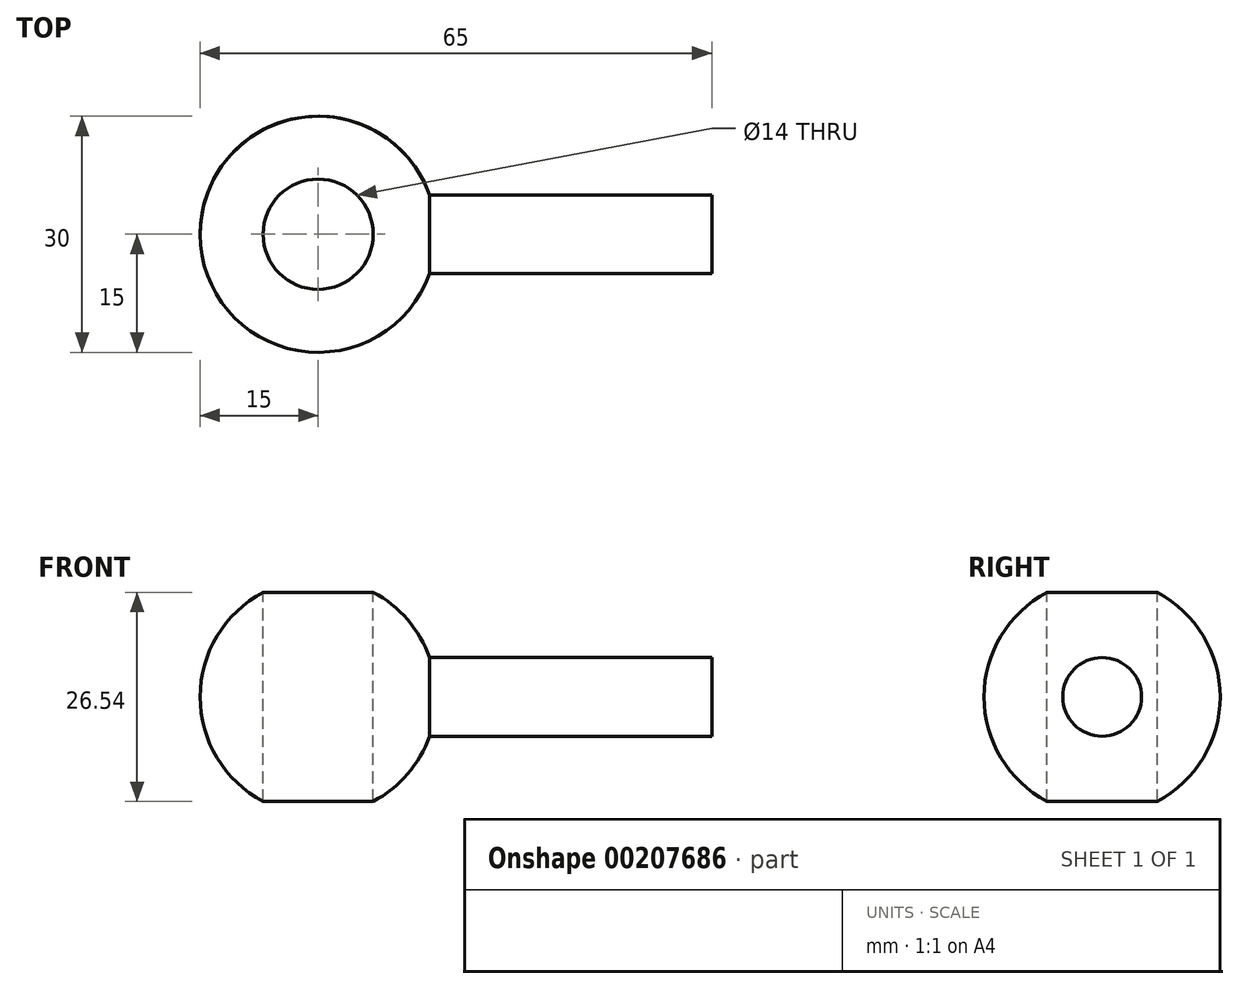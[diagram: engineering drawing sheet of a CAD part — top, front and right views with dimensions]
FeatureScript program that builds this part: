
annotation { "Feature Type Name" : "Feature", "Feature Type Description" : "" }
export const myFeature = defineFeature(function(context is Context, id is Id, definition is map)
    precondition{}
    {
        {
            var Q0;
            Q0=qCreatedBy(makeId("Top.planeOp"),FACE);
            var sketch = newSketch(context, id + "F0", { "sketchPlane" : qUnion([Q0])});
            skArc(sketch, "E0", {"start": v(15, 0) * mm, "mid": v(0, 15) * mm, "end": v(-15, 0) * mm});
            skLineSegment(sketch, "E1", {"start": v(0, 0) * mm, "end": v(50, 0) * mm});
            skLineSegment(sketch, "E2", {"start": v(50, 5) * mm, "end": v(50, 0) * mm});
            skLineSegment(sketch, "E3", {"start": v(50, 5) * mm, "end": v(14.14, 5) * mm});
            skLineSegment(sketch, "E4", {"start": v(-15, 0) * mm, "end": v(0, 0) * mm});
            skSolve(sketch);
        }
        {
            var Q0;
            {var subQ4=sQuery(id+"F0.wireOp",EDGE,"E4");Q0=makeQuery(id+"F0.imprint","IMPRINT",FACE,{"disambiguationData":[TD([[makeQuery(id+"F0.imprint","IMPRINT",EDGE,{"derivedFrom":subQ4}),1.0]])]});}
            var Q1;
            {var subQ4=sQuery(id+"F0.wireOp",EDGE,"E2");Q1=makeQuery(id+"F0.imprint","IMPRINT",FACE,{"disambiguationData":[TD([[makeQuery(id+"F0.imprint","IMPRINT",EDGE,{"derivedFrom":subQ4}),-1.0]])]});}
            var Q2;
            Q2=sQuery(id+"F0.wireOp",EDGE,"E1");
            revolve(context, id + "F1", {"entities" : qUnion([Q0, Q1]), "axis" : qUnion([Q2]), "revolveType" : RevolveType.FULL});
        }
        {
            var Q0;
            Q0=qCreatedBy(makeId("Top.planeOp"),FACE);
            var sketch = newSketch(context, id + "F2", { "sketchPlane" : qUnion([Q0])});
            skCircle(sketch, "E5", {"center": v(0, 0) * mm, "radius": 7 * mm});
            skSolve(sketch);
        }
        {
            var Q0;
            Q0 = qSketchRegion(id + "F2", true);
            extrude(context, id + "F3", {"entities" : qUnion([Q0]), "operationType" : NewBodyOperationType.REMOVE, "endBound" : BoundingType.SYMMETRIC, "oppositeDirection" : true, "depth" : 30 * mm});
        }
    });
